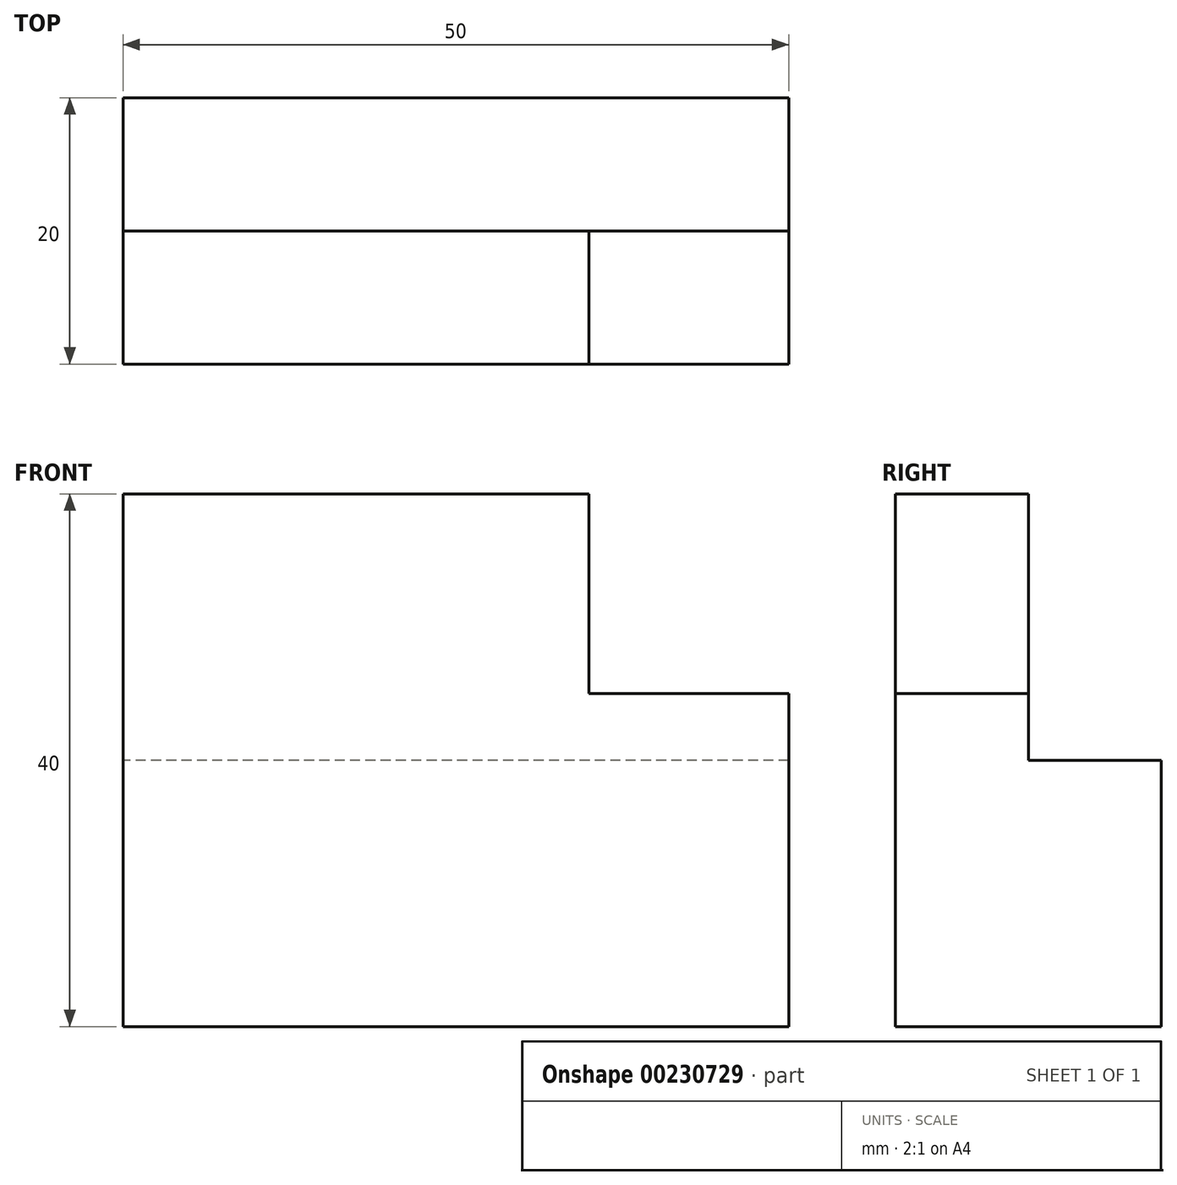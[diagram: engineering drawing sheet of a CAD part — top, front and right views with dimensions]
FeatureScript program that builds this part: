
annotation { "Feature Type Name" : "Feature", "Feature Type Description" : "" }
export const myFeature = defineFeature(function(context is Context, id is Id, definition is map)
    precondition{}
    {
        {
            var Q0;
            Q0=qCreatedBy(makeId("Front.planeOp"),FACE);
            var sketch = newSketch(context, id + "F0", { "sketchPlane" : qUnion([Q0])});
            skLineSegment(sketch, "E0.bottom", {"start": v(-25, 20) * mm, "end": v(25, 20) * mm});
            skLineSegment(sketch, "E0.top", {"start": v(-25, -20) * mm, "end": v(25, -20) * mm});
            skLineSegment(sketch, "E0.left", {"start": v(-25, 20) * mm, "end": v(-25, -20) * mm});
            skLineSegment(sketch, "E0.right", {"start": v(25, 20) * mm, "end": v(25, -20) * mm});
            skPoint(sketch, "E0.middle", {"position": v(0, 0) * mm});
            skSolve(sketch);
        }
        {
            var Q0;
            Q0=makeQuery(id+"F0.imprint","IMPRINT",FACE,{"disambiguationData":[TD([[makeQuery(id+"F0.imprint","IMPRINT",EDGE,{"derivedFrom":sQuery(id+"F0.wireOp",EDGE,"E0.bottom")}),-1.0]])]});
            extrude(context, id + "F1", {"entities" : qUnion([Q0]), "depth" : 10 * mm});
        }
        {
            var Q0;
            Q0=qCreatedBy(makeId("Front.planeOp"),FACE);
            var sketch = newSketch(context, id + "F2", { "sketchPlane" : qUnion([Q0])});
            skLineSegment(sketch, "E1.bottom", {"start": v(10, 20) * mm, "end": v(25, 20) * mm});
            skLineSegment(sketch, "E1.top", {"start": v(10, 5) * mm, "end": v(25, 5) * mm});
            skLineSegment(sketch, "E1.left", {"start": v(10, 20) * mm, "end": v(10, 5) * mm});
            skLineSegment(sketch, "E1.right", {"start": v(25, 20) * mm, "end": v(25, 5) * mm});
            skSolve(sketch);
        }
        {
            var Q0;
            Q0 = qSketchRegion(id + "F2", true);
            extrude(context, id + "F3", {"entities" : qUnion([Q0]), "operationType" : NewBodyOperationType.REMOVE, "endBound" : BoundingType.THROUGH_ALL, "depth" : 25.4 * mm});
        }
        {
            var Q0;
            Q0=qCreatedBy(makeId("Top.planeOp"),FACE);
            var sketch = newSketch(context, id + "F4", { "sketchPlane" : qUnion([Q0])});
            skLineSegment(sketch, "E2.bottom", {"start": v(25, 10) * mm, "end": v(-25, 10) * mm});
            skLineSegment(sketch, "E2.top", {"start": v(25, 0) * mm, "end": v(-25, 0) * mm});
            skLineSegment(sketch, "E2.left", {"start": v(25, 10) * mm, "end": v(25, 0) * mm});
            skLineSegment(sketch, "E2.right", {"start": v(-25, 10) * mm, "end": v(-25, 0) * mm});
            skSolve(sketch);
        }
        {
            var Q0;
            Q0=makeQuery(id+"F4.imprint","IMPRINT",FACE,{"disambiguationData":[TD([[makeQuery(id+"F4.imprint","IMPRINT",EDGE,{"derivedFrom":sQuery(id+"F4.wireOp",EDGE,"E2.bottom")}),1.0]])]});
            extrude(context, id + "F5", {"entities" : qUnion([Q0]), "operationType" : NewBodyOperationType.ADD, "oppositeDirection" : true, "depth" : 20 * mm});
        }
    });
